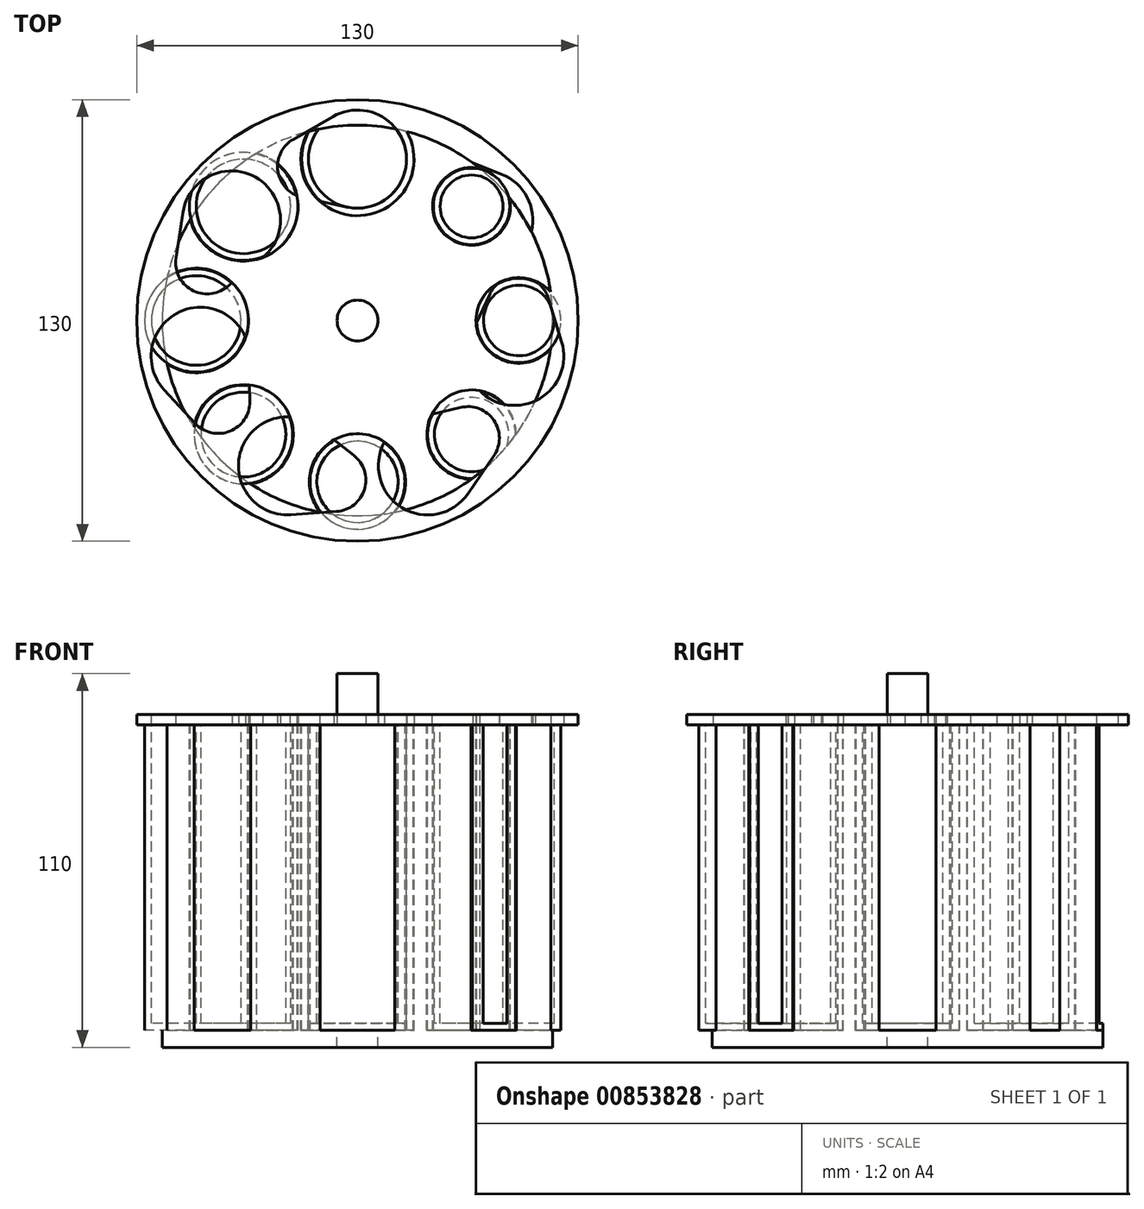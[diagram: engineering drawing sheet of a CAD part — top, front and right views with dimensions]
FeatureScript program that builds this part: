
annotation { "Feature Type Name" : "Feature", "Feature Type Description" : "" }
export const myFeature = defineFeature(function(context is Context, id is Id, definition is map)
    precondition{}
    {
        {
            var Q0;
            Q0=qCreatedBy(makeId("Top.planeOp"),FACE);
            var sketch = newSketch(context, id + "F0", { "sketchPlane" : qUnion([Q0])});
            skCircle(sketch, "E0", {"center": v(0, 0) * mm, "radius": 47.5 * mm});
            skLineSegment(sketch, "E1", {"start": v(0, 0) * mm, "end": v(0, 47.5) * mm, "construction": true});
            skLineSegment(sketch, "E2.1.0", {"start": v(0, 0) * mm, "end": v(33.59, 33.59) * mm, "construction": true});
            skLineSegment(sketch, "E2.2.0", {"start": v(0, 0) * mm, "end": v(47.5, 0) * mm, "construction": true});
            skLineSegment(sketch, "E2.3.0", {"start": v(0, 0) * mm, "end": v(33.59, -33.59) * mm, "construction": true});
            skLineSegment(sketch, "E2.4.0", {"start": v(0, 0) * mm, "end": v(0, -47.5) * mm, "construction": true});
            skLineSegment(sketch, "E2.5.0", {"start": v(0, 0) * mm, "end": v(-33.59, -33.59) * mm, "construction": true});
            skLineSegment(sketch, "E2.6.0", {"start": v(0, 0) * mm, "end": v(-47.5, 0) * mm, "construction": true});
            skLineSegment(sketch, "E2.7.0", {"start": v(0, 0) * mm, "end": v(-33.59, 33.59) * mm, "construction": true});
            skLineSegment(sketch, "E2.anchor2", {"start": v(0, 0) * mm, "end": v(-33.59, 33.59) * mm, "construction": true});
            skCircle(sketch, "E3", {"center": v(0, 47.5) * mm, "radius": 14.45 * mm});
            skCircle(sketch, "E4", {"center": v(33.59, 33.59) * mm, "radius": 9.25 * mm});
            skCircle(sketch, "E5", {"center": v(47.5, 0) * mm, "radius": 10.4 * mm});
            skCircle(sketch, "E6", {"center": v(33.59, -33.59) * mm, "radius": 10.95 * mm});
            skCircle(sketch, "E7", {"center": v(0, -47.5) * mm, "radius": 11.96 * mm});
            skCircle(sketch, "E8", {"center": v(-33.59, -33.59) * mm, "radius": 12.5 * mm});
            skCircle(sketch, "E9", {"center": v(-47.5, 0) * mm, "radius": 13.2 * mm});
            skCircle(sketch, "E10", {"center": v(-33.59, 33.59) * mm, "radius": 13.9 * mm});
            skCircle(sketch, "E11.0", {"center": v(0, 47.5) * mm, "radius": 16.45 * mm});
            skCircle(sketch, "E12.0", {"center": v(33.59, 33.59) * mm, "radius": 11.25 * mm});
            skCircle(sketch, "E13.0", {"center": v(47.5, 0) * mm, "radius": 12.4 * mm});
            skCircle(sketch, "E14.0", {"center": v(33.59, -33.59) * mm, "radius": 12.95 * mm});
            skCircle(sketch, "E15.0", {"center": v(0, -47.5) * mm, "radius": 13.96 * mm});
            skCircle(sketch, "E16.0", {"center": v(-33.59, -33.59) * mm, "radius": 14.5 * mm});
            skCircle(sketch, "E17.0", {"center": v(-47.5, 0) * mm, "radius": 15.2 * mm});
            skCircle(sketch, "E18.0", {"center": v(-33.59, 33.59) * mm, "radius": 15.9 * mm});
            skArc(sketch, "E19.0", {"start": v(-14.53, 55.63) * mm, "mid": v(0, 30.85) * mm, "end": v(14.53, 55.63) * mm});
            skArc(sketch, "E20.0", {"start": v(36.1, 44.76) * mm, "mid": v(25.5, 25.5) * mm, "end": v(44.76, 36.1) * mm});
            skArc(sketch, "E21.0", {"start": v(56.88, 8.41) * mm, "mid": v(34.9, 0) * mm, "end": v(56.88, -8.41) * mm});
            skArc(sketch, "E22.0", {"start": v(46.74, -33.5) * mm, "mid": v(24.29, -24.29) * mm, "end": v(33.5, -46.74) * mm});
            skArc(sketch, "E23.0", {"start": v(10.99, -56.44) * mm, "mid": v(0, -33.34) * mm, "end": v(-10.99, -56.44) * mm});
            skArc(sketch, "E24.0", {"start": v(-31.46, -48.13) * mm, "mid": v(-23.2, -23.2) * mm, "end": v(-48.13, -31.46) * mm});
            skArc(sketch, "E25.0", {"start": v(-56.06, -12.8) * mm, "mid": v(-32.1, 0) * mm, "end": v(-56.06, 12.8) * mm});
            skArc(sketch, "E26.0", {"start": v(-49.22, 29.73) * mm, "mid": v(-22.2, 22.2) * mm, "end": v(-29.73, 49.22) * mm});
            skCircle(sketch, "E27", {"center": v(0, 0) * mm, "radius": 57.5 * mm});
            skSolve(sketch);
        }
        {
            var Q0;
            {var subQ1=sQuery(id+"F0.wireOp",EDGE,"E0");var subQ6=sQuery(id+"F0.wireOp",EDGE,"E21.0");var subQ20=makeQuery(id+"F0.imprint","INTERSECT",VERTEX,{"disambiguationData":[OD(0.0)],"derivedFrom":[subQ1,subQ6]});Q0=makeQuery(id+"F0.imprint","IMPRINT",FACE,{"disambiguationData":[TD([[makeQuery(id+"F0.imprint","IMPRINT",EDGE,{"disambiguationData":[TD([[subQ20,-1.0]])],"derivedFrom":subQ1}),1.0]])]});}
            var Q1;
            {var subQ0=sQuery(id+"F0.wireOp",EDGE,"E26.0");var subQ1=sQuery(id+"F0.wireOp",EDGE,"E0");var subQ2=makeQuery(id+"F0.imprint","INTERSECT",VERTEX,{"disambiguationData":[OD(1.0)],"derivedFrom":[subQ1,subQ0]});Q1=makeQuery(id+"F0.imprint","IMPRINT",FACE,{"disambiguationData":[TD([[makeQuery(id+"F0.imprint","IMPRINT",EDGE,{"disambiguationData":[TD([[subQ2,-1.0]])],"derivedFrom":subQ1}),-1.0]])]});}
            var Q2;
            {var subQ0=sQuery(id+"F0.wireOp",EDGE,"E19.0");var subQ1=sQuery(id+"F0.wireOp",EDGE,"E0");var subQ2=makeQuery(id+"F0.imprint","INTERSECT",VERTEX,{"disambiguationData":[OD(1.0)],"derivedFrom":[subQ1,subQ0]});Q2=makeQuery(id+"F0.imprint","IMPRINT",FACE,{"disambiguationData":[TD([[makeQuery(id+"F0.imprint","IMPRINT",EDGE,{"disambiguationData":[TD([[subQ2,-1.0]])],"derivedFrom":subQ1}),-1.0]])]});}
            var Q3;
            {var subQ0=sQuery(id+"F0.wireOp",EDGE,"E20.0");var subQ1=sQuery(id+"F0.wireOp",EDGE,"E0");var subQ2=makeQuery(id+"F0.imprint","INTERSECT",VERTEX,{"disambiguationData":[OD(1.0)],"derivedFrom":[subQ1,subQ0]});Q3=makeQuery(id+"F0.imprint","IMPRINT",FACE,{"disambiguationData":[TD([[makeQuery(id+"F0.imprint","IMPRINT",EDGE,{"disambiguationData":[TD([[subQ2,-1.0]])],"derivedFrom":subQ1}),-1.0]])]});}
            var Q4;
            {var subQ0=sQuery(id+"F0.wireOp",EDGE,"E21.0");var subQ1=sQuery(id+"F0.wireOp",EDGE,"E0");var subQ2=makeQuery(id+"F0.imprint","INTERSECT",VERTEX,{"disambiguationData":[OD(0.0)],"derivedFrom":[subQ1,subQ0]});Q4=makeQuery(id+"F0.imprint","IMPRINT",FACE,{"disambiguationData":[TD([[makeQuery(id+"F0.imprint","IMPRINT",EDGE,{"disambiguationData":[TD([[subQ2,-1.0]])],"derivedFrom":subQ1}),-1.0]])]});}
            var Q5;
            {var subQ0=sQuery(id+"F0.wireOp",EDGE,"E22.0");var subQ1=sQuery(id+"F0.wireOp",EDGE,"E0");var subQ2=makeQuery(id+"F0.imprint","INTERSECT",VERTEX,{"disambiguationData":[OD(1.0)],"derivedFrom":[subQ1,subQ0]});Q5=makeQuery(id+"F0.imprint","IMPRINT",FACE,{"disambiguationData":[TD([[makeQuery(id+"F0.imprint","IMPRINT",EDGE,{"disambiguationData":[TD([[subQ2,-1.0]])],"derivedFrom":subQ1}),-1.0]])]});}
            var Q6;
            {var subQ0=sQuery(id+"F0.wireOp",EDGE,"E23.0");var subQ1=sQuery(id+"F0.wireOp",EDGE,"E0");var subQ2=makeQuery(id+"F0.imprint","INTERSECT",VERTEX,{"disambiguationData":[OD(1.0)],"derivedFrom":[subQ1,subQ0]});Q6=makeQuery(id+"F0.imprint","IMPRINT",FACE,{"disambiguationData":[TD([[makeQuery(id+"F0.imprint","IMPRINT",EDGE,{"disambiguationData":[TD([[subQ2,-1.0]])],"derivedFrom":subQ1}),-1.0]])]});}
            var Q7;
            {var subQ0=sQuery(id+"F0.wireOp",EDGE,"E24.0");var subQ1=sQuery(id+"F0.wireOp",EDGE,"E0");var subQ2=makeQuery(id+"F0.imprint","INTERSECT",VERTEX,{"disambiguationData":[OD(1.0)],"derivedFrom":[subQ1,subQ0]});Q7=makeQuery(id+"F0.imprint","IMPRINT",FACE,{"disambiguationData":[TD([[makeQuery(id+"F0.imprint","IMPRINT",EDGE,{"disambiguationData":[TD([[subQ2,-1.0]])],"derivedFrom":subQ1}),-1.0]])]});}
            var Q8;
            {var subQ0=sQuery(id+"F0.wireOp",EDGE,"E25.0");var subQ1=sQuery(id+"F0.wireOp",EDGE,"E0");var subQ2=makeQuery(id+"F0.imprint","INTERSECT",VERTEX,{"disambiguationData":[OD(1.0)],"derivedFrom":[subQ1,subQ0]});Q8=makeQuery(id+"F0.imprint","IMPRINT",FACE,{"disambiguationData":[TD([[makeQuery(id+"F0.imprint","IMPRINT",EDGE,{"disambiguationData":[TD([[subQ2,-1.0]])],"derivedFrom":subQ1}),-1.0]])]});}
            extrude(context, id + "F1", {"entities" : qUnion([Q0, Q1, Q2, Q3, Q4, Q5, Q6, Q7, Q8]), "oppositeDirection" : true, "depth" : 90 * mm, "offsetDistance" : 25 * mm});
        }
        {
            var Q0;
            Q0=makeQuery(id+"F1.opExtrude","CAP_FACE",FACE,{"disambiguationData":[OSD([sQuery(id+"F0.wireOp",EDGE,"E19.0"),sQuery(id+"F0.wireOp",EDGE,"E20.0"),sQuery(id+"F0.wireOp",EDGE,"E21.0"),sQuery(id+"F0.wireOp",EDGE,"E22.0"),sQuery(id+"F0.wireOp",EDGE,"E23.0"),sQuery(id+"F0.wireOp",EDGE,"E24.0"),sQuery(id+"F0.wireOp",EDGE,"E25.0"),sQuery(id+"F0.wireOp",EDGE,"E26.0"),sQuery(id+"F0.wireOp",EDGE,"E27")])],"isStart":true});
            var sketch = newSketch(context, id + "F2", { "sketchPlane" : qUnion([Q0])});
            skCircle(sketch, "E28.0", {"center": v(0, 0) * mm, "radius": 57.5 * mm});
            skCircle(sketch, "E29", {"center": v(0, 0) * mm, "radius": 6 * mm});
            skSolve(sketch);
        }
        {
            var Q0;
            Q0=qSketchRegion(id+"F2",true);
            extrude(context, id + "F3", {"entities" : qUnion([Q0]), "operationType" : NewBodyOperationType.ADD, "oppositeDirection" : true, "depth" : 95 * mm, "offsetDistance" : 25 * mm, "hasSecondDirection" : true, "secondDirectionOppositeDirection" : true, "secondDirectionDepth" : 90 * mm});
        }
        {
            var Q0;
            {var subQ0=sQuery(id+"F0.wireOp",EDGE,"E27");var subQ1=sQuery(id+"F0.wireOp",EDGE,"E3");var subQ2=makeQuery(id+"F0.imprint","INTERSECT",VERTEX,{"disambiguationData":[OD(0.0)],"derivedFrom":[subQ1,subQ0]});Q0=makeQuery(id+"F0.imprint","IMPRINT",FACE,{"disambiguationData":[TD([[makeQuery(id+"F0.imprint","IMPRINT",EDGE,{"disambiguationData":[TD([[subQ2,1.0]])],"derivedFrom":subQ1}),-1.0]])]});}
            var Q1;
            {var subQ0=sQuery(id+"F0.wireOp",EDGE,"E11.0");var subQ1=sQuery(id+"F0.wireOp",EDGE,"E0");var subQ2=makeQuery(id+"F0.imprint","INTERSECT",VERTEX,{"disambiguationData":[OD(0.0)],"derivedFrom":[subQ1,subQ0]});Q1=makeQuery(id+"F0.imprint","IMPRINT",FACE,{"disambiguationData":[TD([[makeQuery(id+"F0.imprint","IMPRINT",EDGE,{"disambiguationData":[TD([[subQ2,-1.0]])],"derivedFrom":subQ1}),1.0]])]});}
            var Q2;
            {var subQ0=sQuery(id+"F0.wireOp",EDGE,"E11.0");var subQ1=sQuery(id+"F0.wireOp",EDGE,"E0");var subQ2=makeQuery(id+"F0.imprint","INTERSECT",VERTEX,{"disambiguationData":[OD(0.0)],"derivedFrom":[subQ1,subQ0]});Q2=makeQuery(id+"F0.imprint","IMPRINT",FACE,{"disambiguationData":[TD([[makeQuery(id+"F0.imprint","IMPRINT",EDGE,{"disambiguationData":[TD([[subQ2,-1.0]])],"derivedFrom":subQ1}),-1.0]])]});}
            var Q3;
            {var subQ0=sQuery(id+"F0.wireOp",EDGE,"E3");var subQ1=sQuery(id+"F0.wireOp",EDGE,"E0");var subQ2=makeQuery(id+"F0.imprint","INTERSECT",VERTEX,{"disambiguationData":[OD(1.0)],"derivedFrom":[subQ1,subQ0]});Q3=makeQuery(id+"F0.imprint","IMPRINT",FACE,{"disambiguationData":[TD([[makeQuery(id+"F0.imprint","IMPRINT",EDGE,{"disambiguationData":[TD([[subQ2,-1.0]])],"derivedFrom":subQ1}),-1.0]])]});}
            var Q4;
            {var subQ1=sQuery(id+"F0.wireOp",EDGE,"E12.0");var subQ3=sQuery(id+"F0.wireOp",EDGE,"E0");var subQ9=makeQuery(id+"F0.imprint","INTERSECT",VERTEX,{"disambiguationData":[OD(0.0)],"derivedFrom":[subQ3,subQ1]});Q4=makeQuery(id+"F0.imprint","IMPRINT",FACE,{"disambiguationData":[TD([[makeQuery(id+"F0.imprint","IMPRINT",EDGE,{"disambiguationData":[TD([[subQ9,-1.0]])],"derivedFrom":subQ3}),-1.0]])]});}
            var Q5;
            {var subQ0=sQuery(id+"F0.wireOp",EDGE,"E12.0");var subQ1=sQuery(id+"F0.wireOp",EDGE,"E0");var subQ2=makeQuery(id+"F0.imprint","INTERSECT",VERTEX,{"disambiguationData":[OD(0.0)],"derivedFrom":[subQ1,subQ0]});Q5=makeQuery(id+"F0.imprint","IMPRINT",FACE,{"disambiguationData":[TD([[makeQuery(id+"F0.imprint","IMPRINT",EDGE,{"disambiguationData":[TD([[subQ2,-1.0]])],"derivedFrom":subQ1}),1.0]])]});}
            var Q6;
            {var subQ0=sQuery(id+"F0.wireOp",EDGE,"E27");var subQ1=sQuery(id+"F0.wireOp",EDGE,"E12.0");var subQ2=makeQuery(id+"F0.imprint","INTERSECT",VERTEX,{"disambiguationData":[OD(0.0)],"derivedFrom":[subQ1,subQ0]});Q6=makeQuery(id+"F0.imprint","IMPRINT",FACE,{"disambiguationData":[TD([[makeQuery(id+"F0.imprint","IMPRINT",EDGE,{"disambiguationData":[TD([[subQ2,1.0]])],"derivedFrom":subQ1}),1.0]])]});}
            var Q7;
            {var subQ0=sQuery(id+"F0.wireOp",EDGE,"E27");var subQ1=sQuery(id+"F0.wireOp",EDGE,"E5");var subQ2=makeQuery(id+"F0.imprint","INTERSECT",VERTEX,{"disambiguationData":[OD(0.0)],"derivedFrom":[subQ1,subQ0]});Q7=makeQuery(id+"F0.imprint","IMPRINT",FACE,{"disambiguationData":[TD([[makeQuery(id+"F0.imprint","IMPRINT",EDGE,{"disambiguationData":[TD([[subQ2,1.0]])],"derivedFrom":subQ1}),-1.0]])]});}
            var Q8;
            {var subQ0=sQuery(id+"F0.wireOp",EDGE,"E13.0");var subQ1=sQuery(id+"F0.wireOp",EDGE,"E0");var subQ2=makeQuery(id+"F0.imprint","INTERSECT",VERTEX,{"disambiguationData":[OD(0.0)],"derivedFrom":[subQ1,subQ0]});Q8=makeQuery(id+"F0.imprint","IMPRINT",FACE,{"disambiguationData":[TD([[makeQuery(id+"F0.imprint","IMPRINT",EDGE,{"disambiguationData":[TD([[subQ2,1.0]])],"derivedFrom":subQ1}),-1.0]])]});}
            var Q9;
            {var subQ0=sQuery(id+"F0.wireOp",EDGE,"E13.0");var subQ1=sQuery(id+"F0.wireOp",EDGE,"E0");var subQ2=makeQuery(id+"F0.imprint","INTERSECT",VERTEX,{"disambiguationData":[OD(1.0)],"derivedFrom":[subQ1,subQ0]});Q9=makeQuery(id+"F0.imprint","IMPRINT",FACE,{"disambiguationData":[TD([[makeQuery(id+"F0.imprint","IMPRINT",EDGE,{"disambiguationData":[TD([[subQ2,-1.0]])],"derivedFrom":subQ1}),-1.0]])]});}
            var Q10;
            {var subQ0=sQuery(id+"F0.wireOp",EDGE,"E13.0");var subQ1=sQuery(id+"F0.wireOp",EDGE,"E0");var subQ2=makeQuery(id+"F0.imprint","INTERSECT",VERTEX,{"disambiguationData":[OD(0.0)],"derivedFrom":[subQ1,subQ0]});Q10=makeQuery(id+"F0.imprint","IMPRINT",FACE,{"disambiguationData":[TD([[makeQuery(id+"F0.imprint","IMPRINT",EDGE,{"disambiguationData":[TD([[subQ2,1.0]])],"derivedFrom":subQ1}),1.0]])]});}
            var Q11;
            {var subQ0=sQuery(id+"F0.wireOp",EDGE,"E6");var subQ1=sQuery(id+"F0.wireOp",EDGE,"E0");var subQ2=makeQuery(id+"F0.imprint","INTERSECT",VERTEX,{"disambiguationData":[OD(1.0)],"derivedFrom":[subQ1,subQ0]});Q11=makeQuery(id+"F0.imprint","IMPRINT",FACE,{"disambiguationData":[TD([[makeQuery(id+"F0.imprint","IMPRINT",EDGE,{"disambiguationData":[TD([[subQ2,-1.0]])],"derivedFrom":subQ1}),-1.0]])]});}
            var Q12;
            {var subQ0=sQuery(id+"F0.wireOp",EDGE,"E14.0");var subQ1=sQuery(id+"F0.wireOp",EDGE,"E0");var subQ2=makeQuery(id+"F0.imprint","INTERSECT",VERTEX,{"disambiguationData":[OD(0.0)],"derivedFrom":[subQ1,subQ0]});Q12=makeQuery(id+"F0.imprint","IMPRINT",FACE,{"disambiguationData":[TD([[makeQuery(id+"F0.imprint","IMPRINT",EDGE,{"disambiguationData":[TD([[subQ2,-1.0]])],"derivedFrom":subQ1}),1.0]])]});}
            var Q13;
            {var subQ0=sQuery(id+"F0.wireOp",EDGE,"E14.0");var subQ1=sQuery(id+"F0.wireOp",EDGE,"E0");var subQ2=makeQuery(id+"F0.imprint","INTERSECT",VERTEX,{"disambiguationData":[OD(0.0)],"derivedFrom":[subQ1,subQ0]});Q13=makeQuery(id+"F0.imprint","IMPRINT",FACE,{"disambiguationData":[TD([[makeQuery(id+"F0.imprint","IMPRINT",EDGE,{"disambiguationData":[TD([[subQ2,-1.0]])],"derivedFrom":subQ1}),-1.0]])]});}
            var Q14;
            {var subQ0=sQuery(id+"F0.wireOp",EDGE,"E27");var subQ1=sQuery(id+"F0.wireOp",EDGE,"E6");var subQ2=makeQuery(id+"F0.imprint","INTERSECT",VERTEX,{"disambiguationData":[OD(0.0)],"derivedFrom":[subQ1,subQ0]});Q14=makeQuery(id+"F0.imprint","IMPRINT",FACE,{"disambiguationData":[TD([[makeQuery(id+"F0.imprint","IMPRINT",EDGE,{"disambiguationData":[TD([[subQ2,-1.0]])],"derivedFrom":subQ1}),-1.0]])]});}
            var Q15;
            {var subQ0=sQuery(id+"F0.wireOp",EDGE,"E27");var subQ1=sQuery(id+"F0.wireOp",EDGE,"E7");var subQ2=makeQuery(id+"F0.imprint","INTERSECT",VERTEX,{"disambiguationData":[OD(0.0)],"derivedFrom":[subQ1,subQ0]});Q15=makeQuery(id+"F0.imprint","IMPRINT",FACE,{"disambiguationData":[TD([[makeQuery(id+"F0.imprint","IMPRINT",EDGE,{"disambiguationData":[TD([[subQ2,-1.0]])],"derivedFrom":subQ1}),-1.0]])]});}
            var Q16;
            {var subQ0=sQuery(id+"F0.wireOp",EDGE,"E7");var subQ1=sQuery(id+"F0.wireOp",EDGE,"E0");var subQ2=makeQuery(id+"F0.imprint","INTERSECT",VERTEX,{"disambiguationData":[OD(1.0)],"derivedFrom":[subQ1,subQ0]});Q16=makeQuery(id+"F0.imprint","IMPRINT",FACE,{"disambiguationData":[TD([[makeQuery(id+"F0.imprint","IMPRINT",EDGE,{"disambiguationData":[TD([[subQ2,-1.0]])],"derivedFrom":subQ1}),-1.0]])]});}
            var Q17;
            {var subQ0=sQuery(id+"F0.wireOp",EDGE,"E15.0");var subQ1=sQuery(id+"F0.wireOp",EDGE,"E0");var subQ2=makeQuery(id+"F0.imprint","INTERSECT",VERTEX,{"disambiguationData":[OD(0.0)],"derivedFrom":[subQ1,subQ0]});Q17=makeQuery(id+"F0.imprint","IMPRINT",FACE,{"disambiguationData":[TD([[makeQuery(id+"F0.imprint","IMPRINT",EDGE,{"disambiguationData":[TD([[subQ2,-1.0]])],"derivedFrom":subQ1}),1.0]])]});}
            var Q18;
            {var subQ0=sQuery(id+"F0.wireOp",EDGE,"E15.0");var subQ1=sQuery(id+"F0.wireOp",EDGE,"E0");var subQ2=makeQuery(id+"F0.imprint","INTERSECT",VERTEX,{"disambiguationData":[OD(0.0)],"derivedFrom":[subQ1,subQ0]});Q18=makeQuery(id+"F0.imprint","IMPRINT",FACE,{"disambiguationData":[TD([[makeQuery(id+"F0.imprint","IMPRINT",EDGE,{"disambiguationData":[TD([[subQ2,-1.0]])],"derivedFrom":subQ1}),-1.0]])]});}
            var Q19;
            {var subQ0=sQuery(id+"F0.wireOp",EDGE,"E27");var subQ1=sQuery(id+"F0.wireOp",EDGE,"E8");var subQ2=makeQuery(id+"F0.imprint","INTERSECT",VERTEX,{"disambiguationData":[OD(0.0)],"derivedFrom":[subQ1,subQ0]});Q19=makeQuery(id+"F0.imprint","IMPRINT",FACE,{"disambiguationData":[TD([[makeQuery(id+"F0.imprint","IMPRINT",EDGE,{"disambiguationData":[TD([[subQ2,-1.0]])],"derivedFrom":subQ1}),-1.0]])]});}
            var Q20;
            {var subQ0=sQuery(id+"F0.wireOp",EDGE,"E8");var subQ1=sQuery(id+"F0.wireOp",EDGE,"E0");var subQ2=makeQuery(id+"F0.imprint","INTERSECT",VERTEX,{"disambiguationData":[OD(1.0)],"derivedFrom":[subQ1,subQ0]});Q20=makeQuery(id+"F0.imprint","IMPRINT",FACE,{"disambiguationData":[TD([[makeQuery(id+"F0.imprint","IMPRINT",EDGE,{"disambiguationData":[TD([[subQ2,-1.0]])],"derivedFrom":subQ1}),-1.0]])]});}
            var Q21;
            {var subQ0=sQuery(id+"F0.wireOp",EDGE,"E16.0");var subQ1=sQuery(id+"F0.wireOp",EDGE,"E0");var subQ2=makeQuery(id+"F0.imprint","INTERSECT",VERTEX,{"disambiguationData":[OD(0.0)],"derivedFrom":[subQ1,subQ0]});Q21=makeQuery(id+"F0.imprint","IMPRINT",FACE,{"disambiguationData":[TD([[makeQuery(id+"F0.imprint","IMPRINT",EDGE,{"disambiguationData":[TD([[subQ2,-1.0]])],"derivedFrom":subQ1}),1.0]])]});}
            var Q22;
            {var subQ0=sQuery(id+"F0.wireOp",EDGE,"E16.0");var subQ1=sQuery(id+"F0.wireOp",EDGE,"E0");var subQ2=makeQuery(id+"F0.imprint","INTERSECT",VERTEX,{"disambiguationData":[OD(0.0)],"derivedFrom":[subQ1,subQ0]});Q22=makeQuery(id+"F0.imprint","IMPRINT",FACE,{"disambiguationData":[TD([[makeQuery(id+"F0.imprint","IMPRINT",EDGE,{"disambiguationData":[TD([[subQ2,-1.0]])],"derivedFrom":subQ1}),-1.0]])]});}
            var Q23;
            {var subQ0=sQuery(id+"F0.wireOp",EDGE,"E27");var subQ1=sQuery(id+"F0.wireOp",EDGE,"E9");var subQ2=makeQuery(id+"F0.imprint","INTERSECT",VERTEX,{"disambiguationData":[OD(0.0)],"derivedFrom":[subQ1,subQ0]});Q23=makeQuery(id+"F0.imprint","IMPRINT",FACE,{"disambiguationData":[TD([[makeQuery(id+"F0.imprint","IMPRINT",EDGE,{"disambiguationData":[TD([[subQ2,-1.0]])],"derivedFrom":subQ1}),-1.0]])]});}
            var Q24;
            {var subQ0=sQuery(id+"F0.wireOp",EDGE,"E9");var subQ1=sQuery(id+"F0.wireOp",EDGE,"E0");var subQ2=makeQuery(id+"F0.imprint","INTERSECT",VERTEX,{"disambiguationData":[OD(1.0)],"derivedFrom":[subQ1,subQ0]});Q24=makeQuery(id+"F0.imprint","IMPRINT",FACE,{"disambiguationData":[TD([[makeQuery(id+"F0.imprint","IMPRINT",EDGE,{"disambiguationData":[TD([[subQ2,-1.0]])],"derivedFrom":subQ1}),-1.0]])]});}
            var Q25;
            {var subQ0=sQuery(id+"F0.wireOp",EDGE,"E17.0");var subQ1=sQuery(id+"F0.wireOp",EDGE,"E0");var subQ2=makeQuery(id+"F0.imprint","INTERSECT",VERTEX,{"disambiguationData":[OD(0.0)],"derivedFrom":[subQ1,subQ0]});Q25=makeQuery(id+"F0.imprint","IMPRINT",FACE,{"disambiguationData":[TD([[makeQuery(id+"F0.imprint","IMPRINT",EDGE,{"disambiguationData":[TD([[subQ2,-1.0]])],"derivedFrom":subQ1}),1.0]])]});}
            var Q26;
            {var subQ0=sQuery(id+"F0.wireOp",EDGE,"E17.0");var subQ1=sQuery(id+"F0.wireOp",EDGE,"E0");var subQ2=makeQuery(id+"F0.imprint","INTERSECT",VERTEX,{"disambiguationData":[OD(0.0)],"derivedFrom":[subQ1,subQ0]});Q26=makeQuery(id+"F0.imprint","IMPRINT",FACE,{"disambiguationData":[TD([[makeQuery(id+"F0.imprint","IMPRINT",EDGE,{"disambiguationData":[TD([[subQ2,-1.0]])],"derivedFrom":subQ1}),-1.0]])]});}
            var Q27;
            {var subQ0=sQuery(id+"F0.wireOp",EDGE,"E18.0");var subQ1=sQuery(id+"F0.wireOp",EDGE,"E0");var subQ2=makeQuery(id+"F0.imprint","INTERSECT",VERTEX,{"disambiguationData":[OD(0.0)],"derivedFrom":[subQ1,subQ0]});Q27=makeQuery(id+"F0.imprint","IMPRINT",FACE,{"disambiguationData":[TD([[makeQuery(id+"F0.imprint","IMPRINT",EDGE,{"disambiguationData":[TD([[subQ2,-1.0]])],"derivedFrom":subQ1}),1.0]])]});}
            var Q28;
            {var subQ0=sQuery(id+"F0.wireOp",EDGE,"E10");var subQ1=sQuery(id+"F0.wireOp",EDGE,"E0");var subQ2=makeQuery(id+"F0.imprint","INTERSECT",VERTEX,{"disambiguationData":[OD(1.0)],"derivedFrom":[subQ1,subQ0]});Q28=makeQuery(id+"F0.imprint","IMPRINT",FACE,{"disambiguationData":[TD([[makeQuery(id+"F0.imprint","IMPRINT",EDGE,{"disambiguationData":[TD([[subQ2,-1.0]])],"derivedFrom":subQ1}),-1.0]])]});}
            var Q29;
            {var subQ0=sQuery(id+"F0.wireOp",EDGE,"E27");var subQ1=sQuery(id+"F0.wireOp",EDGE,"E10");var subQ2=makeQuery(id+"F0.imprint","INTERSECT",VERTEX,{"disambiguationData":[OD(0.0)],"derivedFrom":[subQ1,subQ0]});Q29=makeQuery(id+"F0.imprint","IMPRINT",FACE,{"disambiguationData":[TD([[makeQuery(id+"F0.imprint","IMPRINT",EDGE,{"disambiguationData":[TD([[subQ2,-1.0]])],"derivedFrom":subQ1}),-1.0]])]});}
            var Q30;
            {var subQ0=sQuery(id+"F0.wireOp",EDGE,"E18.0");var subQ1=sQuery(id+"F0.wireOp",EDGE,"E0");var subQ2=makeQuery(id+"F0.imprint","INTERSECT",VERTEX,{"disambiguationData":[OD(0.0)],"derivedFrom":[subQ1,subQ0]});Q30=makeQuery(id+"F0.imprint","IMPRINT",FACE,{"disambiguationData":[TD([[makeQuery(id+"F0.imprint","IMPRINT",EDGE,{"disambiguationData":[TD([[subQ2,-1.0]])],"derivedFrom":subQ1}),-1.0]])]});}
            var Q31;
            {var subQ0=sQuery(id+"F0.wireOp",EDGE,"E27");var subQ1=sQuery(id+"F0.wireOp",EDGE,"E3");var subQ2=makeQuery(id+"F0.imprint","INTERSECT",VERTEX,{"disambiguationData":[OD(0.0)],"derivedFrom":[subQ1,subQ0]});Q31=makeQuery(id+"F0.imprint","IMPRINT",FACE,{"disambiguationData":[TD([[makeQuery(id+"F0.imprint","IMPRINT",EDGE,{"disambiguationData":[TD([[subQ2,1.0]])],"derivedFrom":subQ1}),1.0]])]});}
            var Q32;
            {var subQ0=sQuery(id+"F0.wireOp",EDGE,"E3");var subQ1=sQuery(id+"F0.wireOp",EDGE,"E0");var subQ2=makeQuery(id+"F0.imprint","INTERSECT",VERTEX,{"disambiguationData":[OD(0.0)],"derivedFrom":[subQ1,subQ0]});Q32=makeQuery(id+"F0.imprint","IMPRINT",FACE,{"disambiguationData":[TD([[makeQuery(id+"F0.imprint","IMPRINT",EDGE,{"disambiguationData":[TD([[subQ2,-1.0]])],"derivedFrom":subQ1}),-1.0]])]});}
            var Q33;
            {var subQ0=sQuery(id+"F0.wireOp",EDGE,"E3");var subQ1=sQuery(id+"F0.wireOp",EDGE,"E0");var subQ2=makeQuery(id+"F0.imprint","INTERSECT",VERTEX,{"disambiguationData":[OD(0.0)],"derivedFrom":[subQ1,subQ0]});Q33=makeQuery(id+"F0.imprint","IMPRINT",FACE,{"disambiguationData":[TD([[makeQuery(id+"F0.imprint","IMPRINT",EDGE,{"disambiguationData":[TD([[subQ2,-1.0]])],"derivedFrom":subQ1}),1.0]])]});}
            var Q34;
            {var subQ0=sQuery(id+"F0.wireOp",EDGE,"E4");var subQ1=sQuery(id+"F0.wireOp",EDGE,"E0");var subQ2=makeQuery(id+"F0.imprint","INTERSECT",VERTEX,{"disambiguationData":[OD(0.0)],"derivedFrom":[subQ1,subQ0]});Q34=makeQuery(id+"F0.imprint","IMPRINT",FACE,{"disambiguationData":[TD([[makeQuery(id+"F0.imprint","IMPRINT",EDGE,{"disambiguationData":[TD([[subQ2,-1.0]])],"derivedFrom":subQ1}),-1.0]])]});}
            var Q35;
            {var subQ0=sQuery(id+"F0.wireOp",EDGE,"E4");var subQ1=sQuery(id+"F0.wireOp",EDGE,"E0");var subQ2=makeQuery(id+"F0.imprint","INTERSECT",VERTEX,{"disambiguationData":[OD(0.0)],"derivedFrom":[subQ1,subQ0]});Q35=makeQuery(id+"F0.imprint","IMPRINT",FACE,{"disambiguationData":[TD([[makeQuery(id+"F0.imprint","IMPRINT",EDGE,{"disambiguationData":[TD([[subQ2,-1.0]])],"derivedFrom":subQ1}),1.0]])]});}
            var Q36;
            {var subQ0=sQuery(id+"F0.wireOp",EDGE,"E5");var subQ1=sQuery(id+"F0.wireOp",EDGE,"E0");var subQ2=makeQuery(id+"F0.imprint","INTERSECT",VERTEX,{"disambiguationData":[OD(0.0)],"derivedFrom":[subQ1,subQ0]});Q36=makeQuery(id+"F0.imprint","IMPRINT",FACE,{"disambiguationData":[TD([[makeQuery(id+"F0.imprint","IMPRINT",EDGE,{"disambiguationData":[TD([[subQ2,1.0]])],"derivedFrom":subQ1}),-1.0]])]});}
            var Q37;
            {var subQ0=sQuery(id+"F0.wireOp",EDGE,"E5");var subQ1=sQuery(id+"F0.wireOp",EDGE,"E0");var subQ2=makeQuery(id+"F0.imprint","INTERSECT",VERTEX,{"disambiguationData":[OD(0.0)],"derivedFrom":[subQ1,subQ0]});Q37=makeQuery(id+"F0.imprint","IMPRINT",FACE,{"disambiguationData":[TD([[makeQuery(id+"F0.imprint","IMPRINT",EDGE,{"disambiguationData":[TD([[subQ2,1.0]])],"derivedFrom":subQ1}),1.0]])]});}
            var Q38;
            {var subQ0=sQuery(id+"F0.wireOp",EDGE,"E27");var subQ1=sQuery(id+"F0.wireOp",EDGE,"E5");var subQ2=makeQuery(id+"F0.imprint","INTERSECT",VERTEX,{"disambiguationData":[OD(0.0)],"derivedFrom":[subQ1,subQ0]});Q38=makeQuery(id+"F0.imprint","IMPRINT",FACE,{"disambiguationData":[TD([[makeQuery(id+"F0.imprint","IMPRINT",EDGE,{"disambiguationData":[TD([[subQ2,1.0]])],"derivedFrom":subQ1}),1.0]])]});}
            var Q39;
            {var subQ0=sQuery(id+"F0.wireOp",EDGE,"E27");var subQ1=sQuery(id+"F0.wireOp",EDGE,"E6");var subQ2=makeQuery(id+"F0.imprint","INTERSECT",VERTEX,{"disambiguationData":[OD(0.0)],"derivedFrom":[subQ1,subQ0]});Q39=makeQuery(id+"F0.imprint","IMPRINT",FACE,{"disambiguationData":[TD([[makeQuery(id+"F0.imprint","IMPRINT",EDGE,{"disambiguationData":[TD([[subQ2,-1.0]])],"derivedFrom":subQ1}),1.0]])]});}
            var Q40;
            {var subQ0=sQuery(id+"F0.wireOp",EDGE,"E6");var subQ1=sQuery(id+"F0.wireOp",EDGE,"E0");var subQ2=makeQuery(id+"F0.imprint","INTERSECT",VERTEX,{"disambiguationData":[OD(0.0)],"derivedFrom":[subQ1,subQ0]});Q40=makeQuery(id+"F0.imprint","IMPRINT",FACE,{"disambiguationData":[TD([[makeQuery(id+"F0.imprint","IMPRINT",EDGE,{"disambiguationData":[TD([[subQ2,-1.0]])],"derivedFrom":subQ1}),-1.0]])]});}
            var Q41;
            {var subQ0=sQuery(id+"F0.wireOp",EDGE,"E6");var subQ1=sQuery(id+"F0.wireOp",EDGE,"E0");var subQ2=makeQuery(id+"F0.imprint","INTERSECT",VERTEX,{"disambiguationData":[OD(0.0)],"derivedFrom":[subQ1,subQ0]});Q41=makeQuery(id+"F0.imprint","IMPRINT",FACE,{"disambiguationData":[TD([[makeQuery(id+"F0.imprint","IMPRINT",EDGE,{"disambiguationData":[TD([[subQ2,-1.0]])],"derivedFrom":subQ1}),1.0]])]});}
            var Q42;
            {var subQ0=sQuery(id+"F0.wireOp",EDGE,"E27");var subQ1=sQuery(id+"F0.wireOp",EDGE,"E7");var subQ2=makeQuery(id+"F0.imprint","INTERSECT",VERTEX,{"disambiguationData":[OD(0.0)],"derivedFrom":[subQ1,subQ0]});Q42=makeQuery(id+"F0.imprint","IMPRINT",FACE,{"disambiguationData":[TD([[makeQuery(id+"F0.imprint","IMPRINT",EDGE,{"disambiguationData":[TD([[subQ2,-1.0]])],"derivedFrom":subQ1}),1.0]])]});}
            var Q43;
            {var subQ0=sQuery(id+"F0.wireOp",EDGE,"E7");var subQ1=sQuery(id+"F0.wireOp",EDGE,"E0");var subQ2=makeQuery(id+"F0.imprint","INTERSECT",VERTEX,{"disambiguationData":[OD(0.0)],"derivedFrom":[subQ1,subQ0]});Q43=makeQuery(id+"F0.imprint","IMPRINT",FACE,{"disambiguationData":[TD([[makeQuery(id+"F0.imprint","IMPRINT",EDGE,{"disambiguationData":[TD([[subQ2,-1.0]])],"derivedFrom":subQ1}),-1.0]])]});}
            var Q44;
            {var subQ0=sQuery(id+"F0.wireOp",EDGE,"E7");var subQ1=sQuery(id+"F0.wireOp",EDGE,"E0");var subQ2=makeQuery(id+"F0.imprint","INTERSECT",VERTEX,{"disambiguationData":[OD(0.0)],"derivedFrom":[subQ1,subQ0]});Q44=makeQuery(id+"F0.imprint","IMPRINT",FACE,{"disambiguationData":[TD([[makeQuery(id+"F0.imprint","IMPRINT",EDGE,{"disambiguationData":[TD([[subQ2,-1.0]])],"derivedFrom":subQ1}),1.0]])]});}
            var Q45;
            {var subQ0=sQuery(id+"F0.wireOp",EDGE,"E27");var subQ1=sQuery(id+"F0.wireOp",EDGE,"E8");var subQ2=makeQuery(id+"F0.imprint","INTERSECT",VERTEX,{"disambiguationData":[OD(0.0)],"derivedFrom":[subQ1,subQ0]});Q45=makeQuery(id+"F0.imprint","IMPRINT",FACE,{"disambiguationData":[TD([[makeQuery(id+"F0.imprint","IMPRINT",EDGE,{"disambiguationData":[TD([[subQ2,-1.0]])],"derivedFrom":subQ1}),1.0]])]});}
            var Q46;
            {var subQ0=sQuery(id+"F0.wireOp",EDGE,"E8");var subQ1=sQuery(id+"F0.wireOp",EDGE,"E0");var subQ2=makeQuery(id+"F0.imprint","INTERSECT",VERTEX,{"disambiguationData":[OD(0.0)],"derivedFrom":[subQ1,subQ0]});Q46=makeQuery(id+"F0.imprint","IMPRINT",FACE,{"disambiguationData":[TD([[makeQuery(id+"F0.imprint","IMPRINT",EDGE,{"disambiguationData":[TD([[subQ2,-1.0]])],"derivedFrom":subQ1}),-1.0]])]});}
            var Q47;
            {var subQ0=sQuery(id+"F0.wireOp",EDGE,"E8");var subQ1=sQuery(id+"F0.wireOp",EDGE,"E0");var subQ2=makeQuery(id+"F0.imprint","INTERSECT",VERTEX,{"disambiguationData":[OD(0.0)],"derivedFrom":[subQ1,subQ0]});Q47=makeQuery(id+"F0.imprint","IMPRINT",FACE,{"disambiguationData":[TD([[makeQuery(id+"F0.imprint","IMPRINT",EDGE,{"disambiguationData":[TD([[subQ2,-1.0]])],"derivedFrom":subQ1}),1.0]])]});}
            var Q48;
            {var subQ0=sQuery(id+"F0.wireOp",EDGE,"E27");var subQ1=sQuery(id+"F0.wireOp",EDGE,"E9");var subQ2=makeQuery(id+"F0.imprint","INTERSECT",VERTEX,{"disambiguationData":[OD(0.0)],"derivedFrom":[subQ1,subQ0]});Q48=makeQuery(id+"F0.imprint","IMPRINT",FACE,{"disambiguationData":[TD([[makeQuery(id+"F0.imprint","IMPRINT",EDGE,{"disambiguationData":[TD([[subQ2,-1.0]])],"derivedFrom":subQ1}),1.0]])]});}
            var Q49;
            {var subQ0=sQuery(id+"F0.wireOp",EDGE,"E9");var subQ1=sQuery(id+"F0.wireOp",EDGE,"E0");var subQ2=makeQuery(id+"F0.imprint","INTERSECT",VERTEX,{"disambiguationData":[OD(0.0)],"derivedFrom":[subQ1,subQ0]});Q49=makeQuery(id+"F0.imprint","IMPRINT",FACE,{"disambiguationData":[TD([[makeQuery(id+"F0.imprint","IMPRINT",EDGE,{"disambiguationData":[TD([[subQ2,-1.0]])],"derivedFrom":subQ1}),-1.0]])]});}
            var Q50;
            {var subQ0=sQuery(id+"F0.wireOp",EDGE,"E9");var subQ1=sQuery(id+"F0.wireOp",EDGE,"E0");var subQ2=makeQuery(id+"F0.imprint","INTERSECT",VERTEX,{"disambiguationData":[OD(0.0)],"derivedFrom":[subQ1,subQ0]});Q50=makeQuery(id+"F0.imprint","IMPRINT",FACE,{"disambiguationData":[TD([[makeQuery(id+"F0.imprint","IMPRINT",EDGE,{"disambiguationData":[TD([[subQ2,-1.0]])],"derivedFrom":subQ1}),1.0]])]});}
            var Q51;
            {var subQ0=sQuery(id+"F0.wireOp",EDGE,"E27");var subQ1=sQuery(id+"F0.wireOp",EDGE,"E10");var subQ2=makeQuery(id+"F0.imprint","INTERSECT",VERTEX,{"disambiguationData":[OD(0.0)],"derivedFrom":[subQ1,subQ0]});Q51=makeQuery(id+"F0.imprint","IMPRINT",FACE,{"disambiguationData":[TD([[makeQuery(id+"F0.imprint","IMPRINT",EDGE,{"disambiguationData":[TD([[subQ2,-1.0]])],"derivedFrom":subQ1}),1.0]])]});}
            var Q52;
            {var subQ0=sQuery(id+"F0.wireOp",EDGE,"E10");var subQ1=sQuery(id+"F0.wireOp",EDGE,"E0");var subQ2=makeQuery(id+"F0.imprint","INTERSECT",VERTEX,{"disambiguationData":[OD(0.0)],"derivedFrom":[subQ1,subQ0]});Q52=makeQuery(id+"F0.imprint","IMPRINT",FACE,{"disambiguationData":[TD([[makeQuery(id+"F0.imprint","IMPRINT",EDGE,{"disambiguationData":[TD([[subQ2,-1.0]])],"derivedFrom":subQ1}),-1.0]])]});}
            var Q53;
            {var subQ0=sQuery(id+"F0.wireOp",EDGE,"E10");var subQ1=sQuery(id+"F0.wireOp",EDGE,"E0");var subQ2=makeQuery(id+"F0.imprint","INTERSECT",VERTEX,{"disambiguationData":[OD(0.0)],"derivedFrom":[subQ1,subQ0]});Q53=makeQuery(id+"F0.imprint","IMPRINT",FACE,{"disambiguationData":[TD([[makeQuery(id+"F0.imprint","IMPRINT",EDGE,{"disambiguationData":[TD([[subQ2,-1.0]])],"derivedFrom":subQ1}),1.0]])]});}
            extrude(context, id + "F4", {"entities" : qUnion([Q0, Q1, Q2, Q3, Q4, Q5, Q6, Q7, Q8, Q9, Q10, Q11, Q12, Q13, Q14, Q15, Q16, Q17, Q18, Q19, Q20, Q21, Q22, Q23, Q24, Q25, Q26, Q27, Q28, Q29, Q30, Q31, Q32, Q33, Q34, Q35, Q36, Q37, Q38, Q39, Q40, Q41, Q42, Q43, Q44, Q45, Q46, Q47, Q48, Q49, Q50, Q51, Q52, Q53]), "oppositeDirection" : true, "depth" : 90 * mm, "offsetDistance" : 25 * mm});
        }
        {
            var Q0;
            {var subQ0=sQuery(id+"F0.wireOp",EDGE,"E27");var subQ1=sQuery(id+"F0.wireOp",EDGE,"E6");var subQ2=makeQuery(id+"F0.imprint","INTERSECT",VERTEX,{"disambiguationData":[OD(0.0)],"derivedFrom":[subQ1,subQ0]});Q0=makeQuery(id+"F0.imprint","IMPRINT",FACE,{"disambiguationData":[TD([[makeQuery(id+"F0.imprint","IMPRINT",EDGE,{"disambiguationData":[TD([[subQ2,-1.0]])],"derivedFrom":subQ1}),1.0]])]});}
            var Q1;
            {var subQ0=sQuery(id+"F0.wireOp",EDGE,"E6");var subQ1=sQuery(id+"F0.wireOp",EDGE,"E0");var subQ2=makeQuery(id+"F0.imprint","INTERSECT",VERTEX,{"disambiguationData":[OD(0.0)],"derivedFrom":[subQ1,subQ0]});Q1=makeQuery(id+"F0.imprint","IMPRINT",FACE,{"disambiguationData":[TD([[makeQuery(id+"F0.imprint","IMPRINT",EDGE,{"disambiguationData":[TD([[subQ2,-1.0]])],"derivedFrom":subQ1}),-1.0]])]});}
            var Q2;
            {var subQ0=sQuery(id+"F0.wireOp",EDGE,"E6");var subQ1=sQuery(id+"F0.wireOp",EDGE,"E0");var subQ2=makeQuery(id+"F0.imprint","INTERSECT",VERTEX,{"disambiguationData":[OD(0.0)],"derivedFrom":[subQ1,subQ0]});Q2=makeQuery(id+"F0.imprint","IMPRINT",FACE,{"disambiguationData":[TD([[makeQuery(id+"F0.imprint","IMPRINT",EDGE,{"disambiguationData":[TD([[subQ2,-1.0]])],"derivedFrom":subQ1}),1.0]])]});}
            var Q3;
            {var subQ0=sQuery(id+"F0.wireOp",EDGE,"E27");var subQ1=sQuery(id+"F0.wireOp",EDGE,"E7");var subQ2=makeQuery(id+"F0.imprint","INTERSECT",VERTEX,{"disambiguationData":[OD(0.0)],"derivedFrom":[subQ1,subQ0]});Q3=makeQuery(id+"F0.imprint","IMPRINT",FACE,{"disambiguationData":[TD([[makeQuery(id+"F0.imprint","IMPRINT",EDGE,{"disambiguationData":[TD([[subQ2,-1.0]])],"derivedFrom":subQ1}),1.0]])]});}
            var Q4;
            {var subQ0=sQuery(id+"F0.wireOp",EDGE,"E7");var subQ1=sQuery(id+"F0.wireOp",EDGE,"E0");var subQ2=makeQuery(id+"F0.imprint","INTERSECT",VERTEX,{"disambiguationData":[OD(0.0)],"derivedFrom":[subQ1,subQ0]});Q4=makeQuery(id+"F0.imprint","IMPRINT",FACE,{"disambiguationData":[TD([[makeQuery(id+"F0.imprint","IMPRINT",EDGE,{"disambiguationData":[TD([[subQ2,-1.0]])],"derivedFrom":subQ1}),-1.0]])]});}
            var Q5;
            {var subQ0=sQuery(id+"F0.wireOp",EDGE,"E7");var subQ1=sQuery(id+"F0.wireOp",EDGE,"E0");var subQ2=makeQuery(id+"F0.imprint","INTERSECT",VERTEX,{"disambiguationData":[OD(0.0)],"derivedFrom":[subQ1,subQ0]});Q5=makeQuery(id+"F0.imprint","IMPRINT",FACE,{"disambiguationData":[TD([[makeQuery(id+"F0.imprint","IMPRINT",EDGE,{"disambiguationData":[TD([[subQ2,-1.0]])],"derivedFrom":subQ1}),1.0]])]});}
            var Q6;
            {var subQ0=sQuery(id+"F0.wireOp",EDGE,"E27");var subQ1=sQuery(id+"F0.wireOp",EDGE,"E8");var subQ2=makeQuery(id+"F0.imprint","INTERSECT",VERTEX,{"disambiguationData":[OD(0.0)],"derivedFrom":[subQ1,subQ0]});Q6=makeQuery(id+"F0.imprint","IMPRINT",FACE,{"disambiguationData":[TD([[makeQuery(id+"F0.imprint","IMPRINT",EDGE,{"disambiguationData":[TD([[subQ2,-1.0]])],"derivedFrom":subQ1}),1.0]])]});}
            var Q7;
            {var subQ0=sQuery(id+"F0.wireOp",EDGE,"E8");var subQ1=sQuery(id+"F0.wireOp",EDGE,"E0");var subQ2=makeQuery(id+"F0.imprint","INTERSECT",VERTEX,{"disambiguationData":[OD(0.0)],"derivedFrom":[subQ1,subQ0]});Q7=makeQuery(id+"F0.imprint","IMPRINT",FACE,{"disambiguationData":[TD([[makeQuery(id+"F0.imprint","IMPRINT",EDGE,{"disambiguationData":[TD([[subQ2,-1.0]])],"derivedFrom":subQ1}),-1.0]])]});}
            var Q8;
            {var subQ0=sQuery(id+"F0.wireOp",EDGE,"E8");var subQ1=sQuery(id+"F0.wireOp",EDGE,"E0");var subQ2=makeQuery(id+"F0.imprint","INTERSECT",VERTEX,{"disambiguationData":[OD(0.0)],"derivedFrom":[subQ1,subQ0]});Q8=makeQuery(id+"F0.imprint","IMPRINT",FACE,{"disambiguationData":[TD([[makeQuery(id+"F0.imprint","IMPRINT",EDGE,{"disambiguationData":[TD([[subQ2,-1.0]])],"derivedFrom":subQ1}),1.0]])]});}
            var Q9;
            {var subQ0=sQuery(id+"F0.wireOp",EDGE,"E27");var subQ1=sQuery(id+"F0.wireOp",EDGE,"E9");var subQ2=makeQuery(id+"F0.imprint","INTERSECT",VERTEX,{"disambiguationData":[OD(0.0)],"derivedFrom":[subQ1,subQ0]});Q9=makeQuery(id+"F0.imprint","IMPRINT",FACE,{"disambiguationData":[TD([[makeQuery(id+"F0.imprint","IMPRINT",EDGE,{"disambiguationData":[TD([[subQ2,-1.0]])],"derivedFrom":subQ1}),1.0]])]});}
            var Q10;
            {var subQ0=sQuery(id+"F0.wireOp",EDGE,"E9");var subQ1=sQuery(id+"F0.wireOp",EDGE,"E0");var subQ2=makeQuery(id+"F0.imprint","INTERSECT",VERTEX,{"disambiguationData":[OD(0.0)],"derivedFrom":[subQ1,subQ0]});Q10=makeQuery(id+"F0.imprint","IMPRINT",FACE,{"disambiguationData":[TD([[makeQuery(id+"F0.imprint","IMPRINT",EDGE,{"disambiguationData":[TD([[subQ2,-1.0]])],"derivedFrom":subQ1}),-1.0]])]});}
            var Q11;
            {var subQ0=sQuery(id+"F0.wireOp",EDGE,"E9");var subQ1=sQuery(id+"F0.wireOp",EDGE,"E0");var subQ2=makeQuery(id+"F0.imprint","INTERSECT",VERTEX,{"disambiguationData":[OD(0.0)],"derivedFrom":[subQ1,subQ0]});Q11=makeQuery(id+"F0.imprint","IMPRINT",FACE,{"disambiguationData":[TD([[makeQuery(id+"F0.imprint","IMPRINT",EDGE,{"disambiguationData":[TD([[subQ2,-1.0]])],"derivedFrom":subQ1}),1.0]])]});}
            var Q12;
            {var subQ0=sQuery(id+"F0.wireOp",EDGE,"E27");var subQ1=sQuery(id+"F0.wireOp",EDGE,"E10");var subQ2=makeQuery(id+"F0.imprint","INTERSECT",VERTEX,{"disambiguationData":[OD(0.0)],"derivedFrom":[subQ1,subQ0]});Q12=makeQuery(id+"F0.imprint","IMPRINT",FACE,{"disambiguationData":[TD([[makeQuery(id+"F0.imprint","IMPRINT",EDGE,{"disambiguationData":[TD([[subQ2,-1.0]])],"derivedFrom":subQ1}),1.0]])]});}
            var Q13;
            {var subQ0=sQuery(id+"F0.wireOp",EDGE,"E10");var subQ1=sQuery(id+"F0.wireOp",EDGE,"E0");var subQ2=makeQuery(id+"F0.imprint","INTERSECT",VERTEX,{"disambiguationData":[OD(0.0)],"derivedFrom":[subQ1,subQ0]});Q13=makeQuery(id+"F0.imprint","IMPRINT",FACE,{"disambiguationData":[TD([[makeQuery(id+"F0.imprint","IMPRINT",EDGE,{"disambiguationData":[TD([[subQ2,-1.0]])],"derivedFrom":subQ1}),-1.0]])]});}
            var Q14;
            {var subQ0=sQuery(id+"F0.wireOp",EDGE,"E10");var subQ1=sQuery(id+"F0.wireOp",EDGE,"E0");var subQ2=makeQuery(id+"F0.imprint","INTERSECT",VERTEX,{"disambiguationData":[OD(0.0)],"derivedFrom":[subQ1,subQ0]});Q14=makeQuery(id+"F0.imprint","IMPRINT",FACE,{"disambiguationData":[TD([[makeQuery(id+"F0.imprint","IMPRINT",EDGE,{"disambiguationData":[TD([[subQ2,-1.0]])],"derivedFrom":subQ1}),1.0]])]});}
            var Q15;
            {var subQ0=sQuery(id+"F0.wireOp",EDGE,"E27");var subQ1=sQuery(id+"F0.wireOp",EDGE,"E3");var subQ2=makeQuery(id+"F0.imprint","INTERSECT",VERTEX,{"disambiguationData":[OD(0.0)],"derivedFrom":[subQ1,subQ0]});Q15=makeQuery(id+"F0.imprint","IMPRINT",FACE,{"disambiguationData":[TD([[makeQuery(id+"F0.imprint","IMPRINT",EDGE,{"disambiguationData":[TD([[subQ2,1.0]])],"derivedFrom":subQ1}),1.0]])]});}
            var Q16;
            {var subQ0=sQuery(id+"F0.wireOp",EDGE,"E3");var subQ1=sQuery(id+"F0.wireOp",EDGE,"E0");var subQ2=makeQuery(id+"F0.imprint","INTERSECT",VERTEX,{"disambiguationData":[OD(0.0)],"derivedFrom":[subQ1,subQ0]});Q16=makeQuery(id+"F0.imprint","IMPRINT",FACE,{"disambiguationData":[TD([[makeQuery(id+"F0.imprint","IMPRINT",EDGE,{"disambiguationData":[TD([[subQ2,-1.0]])],"derivedFrom":subQ1}),-1.0]])]});}
            var Q17;
            {var subQ0=sQuery(id+"F0.wireOp",EDGE,"E3");var subQ1=sQuery(id+"F0.wireOp",EDGE,"E0");var subQ2=makeQuery(id+"F0.imprint","INTERSECT",VERTEX,{"disambiguationData":[OD(0.0)],"derivedFrom":[subQ1,subQ0]});Q17=makeQuery(id+"F0.imprint","IMPRINT",FACE,{"disambiguationData":[TD([[makeQuery(id+"F0.imprint","IMPRINT",EDGE,{"disambiguationData":[TD([[subQ2,-1.0]])],"derivedFrom":subQ1}),1.0]])]});}
            var Q18;
            {var subQ0=sQuery(id+"F0.wireOp",EDGE,"E4");var subQ1=sQuery(id+"F0.wireOp",EDGE,"E0");var subQ2=makeQuery(id+"F0.imprint","INTERSECT",VERTEX,{"disambiguationData":[OD(0.0)],"derivedFrom":[subQ1,subQ0]});Q18=makeQuery(id+"F0.imprint","IMPRINT",FACE,{"disambiguationData":[TD([[makeQuery(id+"F0.imprint","IMPRINT",EDGE,{"disambiguationData":[TD([[subQ2,-1.0]])],"derivedFrom":subQ1}),-1.0]])]});}
            var Q19;
            {var subQ0=sQuery(id+"F0.wireOp",EDGE,"E4");var subQ1=sQuery(id+"F0.wireOp",EDGE,"E0");var subQ2=makeQuery(id+"F0.imprint","INTERSECT",VERTEX,{"disambiguationData":[OD(0.0)],"derivedFrom":[subQ1,subQ0]});Q19=makeQuery(id+"F0.imprint","IMPRINT",FACE,{"disambiguationData":[TD([[makeQuery(id+"F0.imprint","IMPRINT",EDGE,{"disambiguationData":[TD([[subQ2,-1.0]])],"derivedFrom":subQ1}),1.0]])]});}
            var Q20;
            {var subQ0=sQuery(id+"F0.wireOp",EDGE,"E5");var subQ1=sQuery(id+"F0.wireOp",EDGE,"E0");var subQ2=makeQuery(id+"F0.imprint","INTERSECT",VERTEX,{"disambiguationData":[OD(0.0)],"derivedFrom":[subQ1,subQ0]});Q20=makeQuery(id+"F0.imprint","IMPRINT",FACE,{"disambiguationData":[TD([[makeQuery(id+"F0.imprint","IMPRINT",EDGE,{"disambiguationData":[TD([[subQ2,1.0]])],"derivedFrom":subQ1}),1.0]])]});}
            var Q21;
            {var subQ0=sQuery(id+"F0.wireOp",EDGE,"E5");var subQ1=sQuery(id+"F0.wireOp",EDGE,"E0");var subQ2=makeQuery(id+"F0.imprint","INTERSECT",VERTEX,{"disambiguationData":[OD(0.0)],"derivedFrom":[subQ1,subQ0]});Q21=makeQuery(id+"F0.imprint","IMPRINT",FACE,{"disambiguationData":[TD([[makeQuery(id+"F0.imprint","IMPRINT",EDGE,{"disambiguationData":[TD([[subQ2,1.0]])],"derivedFrom":subQ1}),-1.0]])]});}
            var Q22;
            {var subQ0=sQuery(id+"F0.wireOp",EDGE,"E27");var subQ1=sQuery(id+"F0.wireOp",EDGE,"E5");var subQ2=makeQuery(id+"F0.imprint","INTERSECT",VERTEX,{"disambiguationData":[OD(0.0)],"derivedFrom":[subQ1,subQ0]});Q22=makeQuery(id+"F0.imprint","IMPRINT",FACE,{"disambiguationData":[TD([[makeQuery(id+"F0.imprint","IMPRINT",EDGE,{"disambiguationData":[TD([[subQ2,1.0]])],"derivedFrom":subQ1}),1.0]])]});}
            extrude(context, id + "F5", {"entities" : qUnion([Q0, Q1, Q2, Q3, Q4, Q5, Q6, Q7, Q8, Q9, Q10, Q11, Q12, Q13, Q14, Q15, Q16, Q17, Q18, Q19, Q20, Q21, Q22]), "operationType" : NewBodyOperationType.REMOVE, "oppositeDirection" : true, "depth" : 88 * mm, "offsetDistance" : 25 * mm});
        }
        {
            var Q0;
            Q0=makeQuery(id+"F1.opExtrude","CAP_FACE",FACE,{"disambiguationData":[OSD([sQuery(id+"F0.wireOp",EDGE,"E19.0"),sQuery(id+"F0.wireOp",EDGE,"E20.0"),sQuery(id+"F0.wireOp",EDGE,"E21.0"),sQuery(id+"F0.wireOp",EDGE,"E22.0"),sQuery(id+"F0.wireOp",EDGE,"E23.0"),sQuery(id+"F0.wireOp",EDGE,"E24.0"),sQuery(id+"F0.wireOp",EDGE,"E25.0"),sQuery(id+"F0.wireOp",EDGE,"E26.0"),sQuery(id+"F0.wireOp",EDGE,"E27")])],"isStart":true});
            var sketch = newSketch(context, id + "F6", { "sketchPlane" : qUnion([Q0])});
            skCircle(sketch, "E30", {"center": v(0, 0) * mm, "radius": 65 * mm});
            skArc(sketch, "E31.0", {"start": v(-3.09, 33.38) * mm, "mid": v(14.28, 49.7) * mm, "end": v(-7.2, 60.03) * mm});
            skCircle(sketch, "E32.0", {"center": v(0, 0) * mm, "radius": 47.5 * mm, "construction": true});
            skArc(sketch, "E33", {"start": v(-18.88, 53.33) * mm, "mid": v(-23.42, 43.9) * mm, "end": v(-16.26, 36.27) * mm});
            skLineSegment(sketch, "E34", {"start": v(-7.2, 60.03) * mm, "end": v(-18.88, 53.33) * mm});
            skLineSegment(sketch, "E35", {"start": v(-16.26, 36.27) * mm, "end": v(-3.09, 33.38) * mm});
            skLineSegment(sketch, "E36.1.0", {"start": v(-51.42, 31.8) * mm, "end": v(-53.47, 18.48) * mm});
            skArc(sketch, "E36.1.1", {"start": v(-28.03, 18.4) * mm, "mid": v(-29.95, 42.15) * mm, "end": v(-51.42, 31.8) * mm});
            skLineSegment(sketch, "E36.1.2", {"start": v(-38.5, 9.9) * mm, "end": v(-28.03, 18.4) * mm});
            skArc(sketch, "E36.1.3", {"start": v(-53.47, 18.48) * mm, "mid": v(-48.92, 9.05) * mm, "end": v(-38.5, 9.9) * mm});
            skLineSegment(sketch, "E36.2.0", {"start": v(-56.93, -20.37) * mm, "end": v(-47.79, -30.28) * mm});
            skArc(sketch, "E36.2.1", {"start": v(-31.86, -10.44) * mm, "mid": v(-51.63, 2.86) * mm, "end": v(-56.93, -20.37) * mm});
            skLineSegment(sketch, "E36.2.2", {"start": v(-31.74, -23.92) * mm, "end": v(-31.86, -10.44) * mm});
            skArc(sketch, "E36.2.3", {"start": v(-47.79, -30.28) * mm, "mid": v(-37.58, -32.6) * mm, "end": v(-31.74, -23.92) * mm});
            skLineSegment(sketch, "E36.3.0", {"start": v(-19.57, -57.2) * mm, "end": v(-6.12, -56.24) * mm});
            skArc(sketch, "E36.3.1", {"start": v(-11.7, -31.42) * mm, "mid": v(-34.43, -38.58) * mm, "end": v(-19.57, -57.2) * mm});
            skLineSegment(sketch, "E36.3.2", {"start": v(-1.09, -39.73) * mm, "end": v(-11.7, -31.42) * mm});
            skArc(sketch, "E36.3.3", {"start": v(-6.12, -56.24) * mm, "mid": v(2.06, -49.71) * mm, "end": v(-1.09, -39.73) * mm});
            skLineSegment(sketch, "E36.4.0", {"start": v(32.53, -50.97) * mm, "end": v(40.15, -39.85) * mm});
            skArc(sketch, "E36.4.1", {"start": v(17.27, -28.74) * mm, "mid": v(8.7, -50.97) * mm, "end": v(32.53, -50.97) * mm});
            skLineSegment(sketch, "E36.4.2", {"start": v(30.38, -25.62) * mm, "end": v(17.27, -28.74) * mm});
            skArc(sketch, "E36.4.3", {"start": v(40.15, -39.85) * mm, "mid": v(40.15, -29.38) * mm, "end": v(30.38, -25.62) * mm});
            skLineSegment(sketch, "E36.5.0", {"start": v(60.13, -6.35) * mm, "end": v(56.2, 6.55) * mm});
            skArc(sketch, "E36.5.1", {"start": v(33.23, -4.42) * mm, "mid": v(45.27, -24.98) * mm, "end": v(60.13, -6.35) * mm});
            skLineSegment(sketch, "E36.5.2", {"start": v(38.97, 7.78) * mm, "end": v(33.23, -4.42) * mm});
            skArc(sketch, "E36.5.3", {"start": v(56.2, 6.55) * mm, "mid": v(48, 13.07) * mm, "end": v(38.97, 7.78) * mm});
            skLineSegment(sketch, "E36.6.0", {"start": v(42.45, 43.05) * mm, "end": v(29.92, 48.01) * mm});
            skArc(sketch, "E36.6.1", {"start": v(24.17, 23.23) * mm, "mid": v(47.76, 19.82) * mm, "end": v(42.45, 43.05) * mm});
            skLineSegment(sketch, "E36.6.2", {"start": v(18.22, 35.32) * mm, "end": v(24.17, 23.23) * mm});
            skArc(sketch, "E36.6.3", {"start": v(29.92, 48.01) * mm, "mid": v(19.71, 45.68) * mm, "end": v(18.22, 35.32) * mm});
            skCircle(sketch, "E37", {"center": v(0, 0) * mm, "radius": 6.12 * mm});
            skSolve(sketch);
        }
        {
            var Q0;
            Q0=makeQuery(id+"F6.imprint","IMPRINT",FACE,{"disambiguationData":[TD([[makeQuery(id+"F6.imprint","IMPRINT",EDGE,{"derivedFrom":sQuery(id+"F6.wireOp",EDGE,"E30")}),1.0]])]});
            var Q1;
            {var subQ0=sQuery(id+"F6.wireOp",EDGE,"E34");var subQ1=sQuery(id+"F6.wireOp",EDGE,"E33");var subQ2=makeQuery(id+"F6.imprint","INTERSECT",VERTEX,{"derivedFrom":[subQ1,subQ0]});Q1=makeQuery(id+"F6.imprint","IMPRINT",FACE,{"disambiguationData":[TD([[makeQuery(id+"F6.imprint","IMPRINT",EDGE,{"disambiguationData":[TD([[subQ2,-1.0]])],"derivedFrom":subQ1}),-1.0]])]});}
            var Q2;
            {var subQ25=sQuery(id+"F6.wireOp",EDGE,"E36.6.2");Q2=makeQuery(id+"F6.imprint","IMPRINT",FACE,{"disambiguationData":[TD([[makeQuery(id+"F6.imprint","IMPRINT",EDGE,{"derivedFrom":subQ25}),-1.0]])]});}
            var Q3;
            {var subQ0=sQuery(id+"F6.wireOp",EDGE,"E36.5.3");var subQ1=sQuery(id+"F6.wireOp",EDGE,"E36.5.2");var subQ2=makeQuery(id+"F6.imprint","INTERSECT",VERTEX,{"derivedFrom":[subQ1,subQ0]});Q3=makeQuery(id+"F6.imprint","IMPRINT",FACE,{"disambiguationData":[TD([[makeQuery(id+"F6.imprint","IMPRINT",EDGE,{"disambiguationData":[TD([[subQ2,-1.0]])],"derivedFrom":subQ1}),-1.0]])]});}
            var Q4;
            {var subQ0=sQuery(id+"F6.wireOp",EDGE,"E36.4.1");var subQ1=sQuery(id+"F0.wireOp",EDGE,"E23.0");var subQ2=makeQuery(id+"F1.opExtrude","CAP_EDGE",EDGE,{"disambiguationData":[OSD([subQ1])],"isStart":true});var subQ3=makeQuery(id+"F6.imprint","INTERSECT",VERTEX,{"disambiguationData":[OD(1.0)],"derivedFrom":[subQ2,subQ0]});Q4=makeQuery(id+"F6.imprint","IMPRINT",FACE,{"disambiguationData":[TD([[makeQuery(id+"F6.imprint","IMPRINT",EDGE,{"disambiguationData":[TD([[subQ3,-1.0]])],"derivedFrom":subQ0}),-1.0]])]});}
            var Q5;
            {var subQ0=sQuery(id+"F6.wireOp",EDGE,"E36.2.0");var subQ2=sQuery(id+"F0.wireOp",EDGE,"E24.0");var subQ5=makeQuery(id+"F1.opExtrude","CAP_EDGE",EDGE,{"disambiguationData":[OSD([subQ2])],"isStart":true});var subQ6=makeQuery(id+"F6.imprint","INTERSECT",VERTEX,{"derivedFrom":[subQ5,subQ0]});Q5=makeQuery(id+"F6.imprint","IMPRINT",FACE,{"disambiguationData":[TD([[makeQuery(id+"F6.imprint","IMPRINT",EDGE,{"disambiguationData":[TD([[subQ6,1.0]])],"derivedFrom":subQ0}),-1.0]])]});}
            var Q6;
            {var subQ0=sQuery(id+"F6.wireOp",EDGE,"E36.1.3");var subQ1=sQuery(id+"F6.wireOp",EDGE,"E36.1.0");var subQ2=makeQuery(id+"F6.imprint","INTERSECT",VERTEX,{"derivedFrom":[subQ1,subQ0]});Q6=makeQuery(id+"F6.imprint","IMPRINT",FACE,{"disambiguationData":[TD([[makeQuery(id+"F6.imprint","IMPRINT",EDGE,{"disambiguationData":[TD([[subQ2,-1.0]])],"derivedFrom":subQ0}),-1.0]])]});}
            var Q7;
            {var subQ0=sQuery(id+"F6.wireOp",EDGE,"E36.5.1");var subQ1=sQuery(id+"F0.wireOp",EDGE,"E22.0");var subQ2=makeQuery(id+"F1.opExtrude","CAP_EDGE",EDGE,{"disambiguationData":[OSD([subQ1])],"isStart":true});var subQ3=makeQuery(id+"F6.imprint","INTERSECT",VERTEX,{"disambiguationData":[OD(1.0)],"derivedFrom":[subQ2,subQ0]});Q7=makeQuery(id+"F6.imprint","IMPRINT",FACE,{"disambiguationData":[TD([[makeQuery(id+"F6.imprint","IMPRINT",EDGE,{"disambiguationData":[TD([[subQ3,-1.0]])],"derivedFrom":subQ0}),-1.0]])]});}
            extrude(context, id + "F7", {"entities" : qUnion([Q0, Q1, Q2, Q3, Q4, Q5, Q6, Q7]), "depth" : 3 * mm, "offsetDistance" : 25 * mm});
        }
        {
            var Q0;
            Q0=makeQuery(id+"F2.imprint","IMPRINT",FACE,{"disambiguationData":[TD([[makeQuery(id+"F2.imprint","IMPRINT",EDGE,{"derivedFrom":sQuery(id+"F2.wireOp",EDGE,"E29")}),1.0]])]});
            extrude(context, id + "F8", {"entities" : qUnion([Q0]), "operationType" : NewBodyOperationType.ADD, "depth" : 15 * mm, "offsetDistance" : 25 * mm});
        }
    });
